# Revit family: Deca_Cuba de Sobrepor Retangular_L
name_source: partatom
category: Plumbing Fixtures
revit_build: Autodesk Revit 2013 (Build: 20120221_2030(x64)
units: mm (PartAtom-declared; Revit-internal decimal feet)

## types (2) — shared parameters
Aprovado por = Contino/quattroD
Assembly Code = D2010400
Atendimento ao Cliente = 0800-0117073
Criado por = Contino/quattroD
Description = Cuba de sobrepor
Diâmetro Ponto de Esgoto = 40 mm  [stored 0.131234 ft]
Flow Pressure = 0.00 psi
Linha = Cubas de sobrepor
Louça/Metais = Louça
Manufacturer = Deca
Material = Deca_Fireclay
Norma = ABNT NBR 15097-1: 2011 / ABNT NBR 15097-2: 2011
Peso Liquido (Kg) = 10.3
Produto = Cuba de sobrepor Retangular
Raio Ponto de Esgoto = 20 mm  [stored 0.0656168 ft]
Segmento = Luxo
URL = www.deca.com.br/produtos
Variações de COR = Branco (L.1070.17); Ébano (L.1070.95).
Vendido Separadamente = Sifão para lavatório: Cromado: (1680.C.100.112), Dourado (1680.D.100.112).   Slim: Cromado (1684.C.100.112), Dourado (1684.D.100.112) e Gold (1684.D.100.112.GLD).  Quadra: Cromado (1685.C.100.112).                                                                                                                                                                                                                                                                                                                                                                                                                                                                                                  Válvulas de escoamentos compatíveis: Luxo: Cromado (1601.C), Branco (1601.E.BR), Gold (1601.D.GLD); Click: Cromado (1601.C.CLI).  Competitivo: Cromado (1602.C), Dourado (1602.D); Tampão plástico: Cromado (1602.C.PLA).
zero-valued in all types: Default Elevation, WFU

## per-type parameters (varying)
| type | Cuba | Código | Model |
| L.1070.17_Branco Gelo GE17 | Deca GE17 Branco Gelo Cerâmica | L.1070.17 | L.1070.17 |
| L.1070.95_ Ébano EB95 | Deca EB95 Ébano Cerâmica | L.1070.95 | L.1070.95 |

note: [stored X ft] marks values corroborated as IEEE doubles in the binary element streams (Revit-internal decimal feet)

## geometry (parser evidence)
native form markers: Blend x12, Sweep x2
no freeform markers — native parametric forms only
